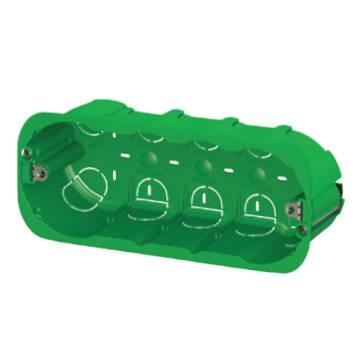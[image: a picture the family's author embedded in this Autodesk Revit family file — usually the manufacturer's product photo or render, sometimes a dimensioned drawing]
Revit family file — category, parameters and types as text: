
# Revit family: Building-FlushMountingEnclosures-GEWISS-24SC-GREENWALL-BOXES_6P
name_source: partatom
category: Apparecchi elettrici
revit_build: Autodesk Revit 2016 (Build: 20161004_0715(x64)
units: mm (PartAtom-declared; Revit-internal decimal feet)

## family parameters
Condiviso = Sì
Host = Superficie
Mantenere orientamento annotazione = Sì
Numero OmniClass = 23.80.30.14.24
Punto di calcolo locali = Sì
Quota connettore circolare = Usa diametro
Taglio con vuoti quando caricato = Sì
Tipo di parte = Normale
Titolo OmniClass = Junction Boxes

## types (1)
- GW24406PM - Halogen free - 6P
    Catalogue = BUILDING
    Catalogue Range = 24SC
    Characteristics = Halogen free
    Compartment pre-arrangement = 3
    Description: = 6 gang
    Descrizione = PLASTERBOARD W. 6 GANG F.M.BOX - GW
    EAN code = 8011564801936
    Electrocod = 0210
    Elementi acciaio = GEWISS - Elementi acciaio
    Fixing supports axles distance = 100MM
    For walls = Plasterboard
    Glow Wire Test = 850°C
    IDF = 35be3827-cff4-4e1c-9667-b323dfbb3906
    IDT = c923a44a-2e51-47f6-a775-de3ee192e6c0
    IP degree = IP40
    Immagine tipo = GW24406PM.jpg
    Installation = Flush mounting enclosures
    Modello = GW24406PM
    No. SYSTEM modules = 6 gang
    Operating temperature = -15 ÷ +60°C
    Outer dim. LxHxD (mm) = 182x73x50
    Produttore = GEWISS S.p.A.
    Prospetto di default = 1219.2 mm  [stored 4 ft]
    SEO = Box
    Scatola = GEWISS - scatola a incasso
    Shock resistance = IK07
    Technical sheet = https://www.gewiss.com
    Thermo-pressure with ball = 70
    Type of material = Halogen free with Standard EN 50267-2-2
    Type: = High capacity
    URL = https://www.gewiss.com
    Version file RFA = 19.0

note: source unit labels omitted for Thermo-pressure with ball — the stored unit's dimension contradicts the parameter name (converter mislabeling)

note: [stored X ft] marks values corroborated as IEEE doubles in the binary element streams (Revit-internal decimal feet)

## geometry (parser evidence)
native form markers: Blend x2, Sweep x3
no freeform markers — native parametric forms only
